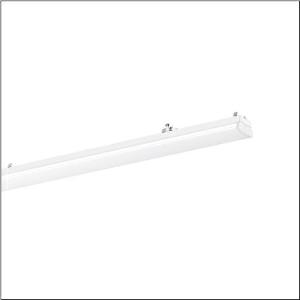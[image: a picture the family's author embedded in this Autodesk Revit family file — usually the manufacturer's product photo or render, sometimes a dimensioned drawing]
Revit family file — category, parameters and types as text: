
# Revit family: licross_r__11_recessed_opal_ho_51tl1dmv4g5m_d39c
name_source: partatom
category: Lighting Fixtures
units: mm (PartAtom-declared; Revit-internal decimal feet)

## family parameters
Cut with Voids When Loaded = No
Host = Face
Light Source = No
Part Type = Normal
Room Calculation Point = No
Round Connector Dimension = Use Diameter
Shared = No

## types (1)
- --- (1 x LED, 16760 lm, 89.2 W, 4000K)
    Apparent Load = 89 VA
    CIE Flux Codes = 44 73 91 87 100
    Color Rendering = 80
    Color Temperature = 4000K
    Default Elevation = 1800 mm
    Description = Licross® 11 recessed opal HO, luminaire insert, of sheet steel, coil coated, white, length: 2.250mm, width: 76mm, height: 87mm, LED rated luminous flux: 16.760lm, light colour: 840, control gear: ON/OFF Multilumen, with plug, 3-pole, with phase selection, mains connection: 220..240V, AC, 50/60Hz, rated input power: 89W, halogen-free wiring, primary optical cover: cover, of PMMA, light emission: direct with ceiling illumination distribution, primary light characteristic: symmetric, protection rating (complete): IP40, insulation class (complete): insulation class I (protective earthing), certification: CE, ENEC, VDE, UKCA, protection symbol: D if used in an environment without relevant dust loads with corresponding accessories, impact resistance: IK06, permissible ambient temperature for indoor applications: -35..+35°C, corresponds to IFS (International Featured Standards) requirements for safety and quality in the food industry, reducing of maximum allowable ambient temperature of 5°C with ceiling mounting, packaging unit: 1 piece
    Height = 83 mm
    Lamp = 1 x LED
    Lamp Light Flux = 16760 lm
    Lamp Power = 89.2 W
    Lamp count = 1
    Length = 2250 mm
    Luminous efficacy = 188 lm/W
    Manufacturer = Siteco
    ModVariant = No
    Model = 51TL1DMV4G5M
    Mounting Place = Ceiling
    Mounting Type = Pendant
    Number of Poles = 1
    OnlyDefault = Yes
    Power Factor = 1
    Product Name = Licross® 11 recessed opal HO
    Product group = luminaire insert
    ProductGroupID = 901
    Protection Class = Protection class I
    Protection Degree = IP 40
    RLX_Detail_Level = 1
    RLX_Emergency_Light_Flux = 0 lm
    RLX_Emergency_Type = 0
    RLX_Emergency_Type_DB = No
    RlxData = <blob elided: 24469 chars, md5=18a91df6>
    Socket = socket
    Standby Power = 0 W
    System Light Flux = 16760 lm
    System Power = 89 W
    Type Comments = factory setting: luminous flux: 100 % | (A | C | E) | 210 mA
    Type Image = l_1313666.jpg
    URL = http://relux.com
    VarID = @adj_044827
    Voltage = 0 V
    Weight = 0.00 kg
    Width = 76 mm

## geometry (parser evidence)
native form markers: Blend x4, Sweep x12
no freeform markers — native parametric forms only
